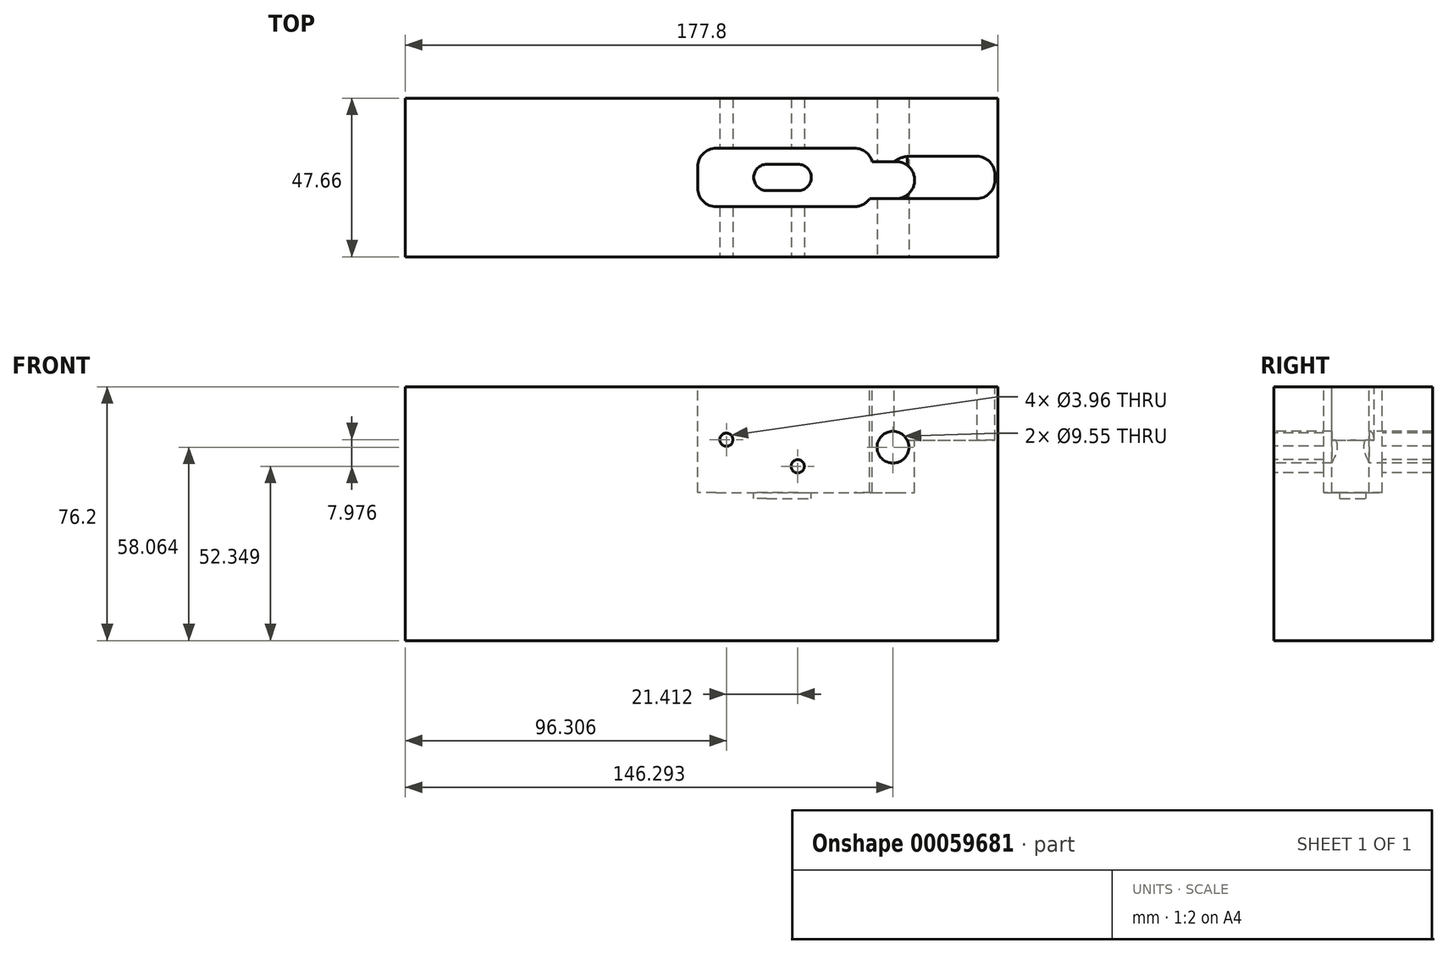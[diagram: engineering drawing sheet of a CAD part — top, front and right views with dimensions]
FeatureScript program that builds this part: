
annotation { "Feature Type Name" : "Feature", "Feature Type Description" : "" }
export const myFeature = defineFeature(function(context is Context, id is Id, definition is map)
    precondition{}
    {
        {
            var Q0;
            Q0=qCreatedBy(makeId("Top.planeOp"),FACE);
            var sketch = newSketch(context, id + "F0", { "sketchPlane" : qUnion([Q0])});
            skLineSegment(sketch, "E0.bottom", {"start": v(0.01, 76.23) * mm, "end": v(177.81, 76.23) * mm});
            skLineSegment(sketch, "E0.top", {"start": v(0.01, 28.58) * mm, "end": v(177.81, 28.58) * mm});
            skLineSegment(sketch, "E0.left", {"start": v(0.01, 76.23) * mm, "end": v(0.01, 28.58) * mm});
            skLineSegment(sketch, "E0.right", {"start": v(177.81, 76.23) * mm, "end": v(177.81, 28.58) * mm});
            skLineSegment(sketch, "E1", {"start": v(177.78, 52.4) * mm, "end": v(-20.58, 52.4) * mm, "construction": true});
            skPoint(sketch, "E1.startSnap0", {"position": v(177.81, 52.4) * mm});
            skPoint(sketch, "E1.endSnap0", {"position": v(0.01, 52.4) * mm});
            skSolve(sketch);
        }
        {
            var Q0;
            Q0=makeQuery(id+"F0.imprint","IMPRINT",FACE,{"disambiguationData":[TD([[makeQuery(id+"F0.imprint","IMPRINT",EDGE,{"derivedFrom":sQuery(id+"F0.wireOp",EDGE,"E0.bottom")}),-1.0]])]});
            extrude(context, id + "F1", {"entities" : qUnion([Q0]), "depth" : 76.2 * mm});
        }
        {
            var Q0;
            Q0=makeQuery(id+"F1.opExtrude","SWEPT_FACE",FACE,{"disambiguationData":[OSD([sQuery(id+"F0.wireOp",EDGE,"E0.top")])]});
            var sketch = newSketch(context, id + "F2", { "sketchPlane" : qUnion([Q0])});
            skCircle(sketch, "E2", {"center": v(166.7, 69.85) * mm, "radius": 3.18 * mm, "construction": true});
            skCircle(sketch, "E3", {"center": v(4.77, 69.85) * mm, "radius": 3.18 * mm, "construction": true});
            skCircle(sketch, "E4", {"center": v(146.3, 58.06) * mm, "radius": 4.78 * mm});
            skCircle(sketch, "E5", {"center": v(117.73, 52.35) * mm, "radius": 1.98 * mm});
            skCircle(sketch, "E6", {"center": v(96.32, 60.33) * mm, "radius": 1.98 * mm});
            skPoint(sketch, "E7", {"position": v(0.01, 76.2) * mm});
            skSolve(sketch);
        }
        {
            var Q0;
            Q0=qSketchRegion(id+"F2",true);
            extrude(context, id + "F3", {"entities" : qUnion([Q0]), "operationType" : NewBodyOperationType.REMOVE, "endBound" : BoundingType.THROUGH_ALL, "oppositeDirection" : true, "depth" : 25.4 * mm});
        }
        {
            var Q0;
            Q0=makeQuery(id+"F1.opExtrude","CAP_FACE",FACE,{"disambiguationData":[OSD([sQuery(id+"F0.wireOp",EDGE,"E0.bottom"),sQuery(id+"F0.wireOp",EDGE,"E0.top"),sQuery(id+"F0.wireOp",EDGE,"E0.left"),sQuery(id+"F0.wireOp",EDGE,"E0.right")])],"isStart":false});
            var sketch = newSketch(context, id + "F4", { "sketchPlane" : qUnion([Q0])});
            skLineSegment(sketch, "E8.right", {"start": v(176.91, 53.21) * mm, "end": v(176.91, 51.59) * mm});
            skPoint(sketch, "E9.visualSharp", {"position": v(176.91, 58.75) * mm});
            skArc(sketch, "E9.filletArc", {"start": v(176.91, 53.21) * mm, "mid": v(175.33, 57.09) * mm, "end": v(171.49, 58.75) * mm});
            skPoint(sketch, "E10.visualSharp", {"position": v(176.91, 46.05) * mm});
            skArc(sketch, "E10.filletArc", {"start": v(171.39, 46.05) * mm, "mid": v(175.3, 47.68) * mm, "end": v(176.91, 51.59) * mm});
            skPoint(sketch, "E11.visualSharp", {"position": v(142.53, 46.05) * mm});
            skLineSegment(sketch, "E12", {"start": v(142.53, 46.05) * mm, "end": v(142.53, 46.05) * mm});
            skLineSegment(sketch, "E13", {"start": v(151.35, 58.75) * mm, "end": v(171.49, 58.75) * mm});
            skLineSegment(sketch, "E14", {"start": v(4.77, 92.25) * mm, "end": v(4.77, 28.58) * mm, "construction": true});
            skLineSegment(sketch, "E15", {"start": v(149.26, 58.75) * mm, "end": v(149.26, 58.75) * mm});
            skLineSegment(sketch, "E16", {"start": v(143.73, 51.13) * mm, "end": v(143.73, 49.23) * mm});
            skLineSegment(sketch, "E17", {"start": v(146.9, 46.05) * mm, "end": v(171.39, 46.05) * mm});
            skPoint(sketch, "E18.visualSharp", {"position": v(143.73, 58.75) * mm});
            skPoint(sketch, "E19.visualSharp", {"position": v(143.73, 46.05) * mm});
            skArc(sketch, "E19.filletArc", {"start": v(143.73, 49.23) * mm, "mid": v(144.66, 46.98) * mm, "end": v(146.9, 46.05) * mm});
            skPoint(sketch, "E20.newPointA", {"position": v(149.26, 58.75) * mm});
            skArc(sketch, "E20.filletArc", {"start": v(151.35, 58.75) * mm, "mid": v(145.96, 56.52) * mm, "end": v(143.73, 51.13) * mm});
            skSolve(sketch);
        }
        {
            var Q0;
            Q0=qSketchRegion(id+"F4",true);
            extrude(context, id + "F5", {"entities" : qUnion([Q0]), "operationType" : NewBodyOperationType.REMOVE, "oppositeDirection" : true, "depth" : 16 * mm});
        }
        {
            var Q0;
            Q0=makeQuery(id+"F1.opExtrude","CAP_FACE",FACE,{"disambiguationData":[OSD([sQuery(id+"F0.wireOp",EDGE,"E0.bottom"),sQuery(id+"F0.wireOp",EDGE,"E0.top"),sQuery(id+"F0.wireOp",EDGE,"E0.left"),sQuery(id+"F0.wireOp",EDGE,"E0.right")])],"isStart":false});
            var sketch = newSketch(context, id + "F6", { "sketchPlane" : qUnion([Q0])});
            skLineSegment(sketch, "E21.bottom", {"start": v(108.48, 56.36) * mm, "end": v(117.83, 56.36) * mm});
            skLineSegment(sketch, "E21.top", {"start": v(108.48, 48.44) * mm, "end": v(117.83, 48.44) * mm});
            skLineSegment(sketch, "E21.left", {"start": v(104.52, 52.4) * mm, "end": v(104.52, 52.4) * mm});
            skLineSegment(sketch, "E21.right", {"start": v(121.8, 52.4) * mm, "end": v(121.8, 52.4) * mm});
            skPoint(sketch, "E22.visualSharp", {"position": v(104.52, 56.36) * mm});
            skArc(sketch, "E22.filletArc", {"start": v(108.48, 56.36) * mm, "mid": v(105.68, 55.2) * mm, "end": v(104.52, 52.4) * mm});
            skPoint(sketch, "E23.visualSharp", {"position": v(121.8, 56.36) * mm});
            skArc(sketch, "E23.filletArc", {"start": v(121.8, 52.4) * mm, "mid": v(120.63, 55.2) * mm, "end": v(117.83, 56.36) * mm});
            skPoint(sketch, "E24.visualSharp", {"position": v(121.8, 48.44) * mm});
            skArc(sketch, "E24.filletArc", {"start": v(117.83, 48.44) * mm, "mid": v(120.63, 49.6) * mm, "end": v(121.8, 52.4) * mm});
            skPoint(sketch, "E25.visualSharp", {"position": v(104.52, 48.44) * mm});
            skArc(sketch, "E25.filletArc", {"start": v(104.52, 52.4) * mm, "mid": v(105.68, 49.6) * mm, "end": v(108.48, 48.44) * mm});
            skSolve(sketch);
        }
        {
            var Q0;
            Q0=qSketchRegion(id+"F6",true);
            extrude(context, id + "F7", {"entities" : qUnion([Q0]), "operationType" : NewBodyOperationType.REMOVE, "oppositeDirection" : true, "depth" : 33.53 * mm});
        }
        {
            var Q0;
            Q0=makeQuery(id+"F1.opExtrude","CAP_FACE",FACE,{"disambiguationData":[OSD([sQuery(id+"F0.wireOp",EDGE,"E0.bottom"),sQuery(id+"F0.wireOp",EDGE,"E0.top"),sQuery(id+"F0.wireOp",EDGE,"E0.left"),sQuery(id+"F0.wireOp",EDGE,"E0.right")])],"isStart":false});
            var sketch = newSketch(context, id + "F8", { "sketchPlane" : qUnion([Q0])});
            skLineSegment(sketch, "E26", {"start": v(-7.04, 52.4) * mm, "end": v(179.84, 52.4) * mm, "construction": true});
            skLineSegment(sketch, "E27.bottom", {"start": v(93.24, 61.16) * mm, "end": v(134.77, 61.16) * mm});
            skLineSegment(sketch, "E27.top", {"start": v(93.24, 43.64) * mm, "end": v(134.77, 43.64) * mm});
            skLineSegment(sketch, "E27.left", {"start": v(87.7, 55.63) * mm, "end": v(87.7, 49.17) * mm});
            skLineSegment(sketch, "E27.right", {"start": v(140.3, 55.63) * mm, "end": v(140.3, 49.17) * mm});
            skLineSegment(sketch, "E28.left", {"start": v(152.8, 51.59) * mm, "end": v(152.8, 51.64) * mm});
            skLineSegment(sketch, "E28.right", {"start": v(129.37, 51.59) * mm, "end": v(129.37, 51.64) * mm});
            skPoint(sketch, "E29.visualSharp", {"position": v(140.3, 61.16) * mm});
            skArc(sketch, "E29.filletArc", {"start": v(140.3, 55.63) * mm, "mid": v(138.69, 59.54) * mm, "end": v(134.77, 61.16) * mm});
            skPoint(sketch, "E30.visualSharp", {"position": v(140.3, 43.64) * mm});
            skArc(sketch, "E30.filletArc", {"start": v(134.77, 43.64) * mm, "mid": v(138.69, 45.26) * mm, "end": v(140.3, 49.17) * mm});
            skPoint(sketch, "E31.visualSharp", {"position": v(87.7, 61.16) * mm});
            skArc(sketch, "E31.filletArc", {"start": v(93.24, 61.16) * mm, "mid": v(89.33, 59.54) * mm, "end": v(87.7, 55.63) * mm});
            skPoint(sketch, "E32.visualSharp", {"position": v(87.7, 43.64) * mm});
            skArc(sketch, "E32.filletArc", {"start": v(87.7, 49.17) * mm, "mid": v(89.33, 45.26) * mm, "end": v(93.24, 43.64) * mm});
            skSolve(sketch);
        }
        {
            var Q0;
            Q0=qSketchRegion(id+"F8",true);
            extrude(context, id + "F9", {"entities" : qUnion([Q0]), "operationType" : NewBodyOperationType.REMOVE, "oppositeDirection" : true, "depth" : 31.72 * mm});
        }
        {
            var Q0;
            Q0=makeQuery(id+"F8.imprint","IMPRINT",FACE,{"disambiguationData":[TD([[makeQuery(id+"F8.imprint","IMPRINT",EDGE,{"derivedFrom":sQuery(id+"F8.wireOp",EDGE,"E27.bottom")}),1.0]])]});
            var sketch = newSketch(context, id + "F10", { "sketchPlane" : qUnion([Q0])});
            skLineSegment(sketch, "E33.bottom", {"start": v(139.35, 57.18) * mm, "end": v(147.24, 57.18) * mm});
            skLineSegment(sketch, "E33.top", {"start": v(139.35, 46.05) * mm, "end": v(147.24, 46.05) * mm});
            skLineSegment(sketch, "E33.left", {"start": v(136.17, 54) * mm, "end": v(136.17, 49.23) * mm});
            skLineSegment(sketch, "E33.right", {"start": v(152.78, 51.64) * mm, "end": v(152.78, 51.59) * mm});
            skPoint(sketch, "E34.visualSharp", {"position": v(152.78, 57.18) * mm});
            skArc(sketch, "E34.filletArc", {"start": v(152.78, 51.64) * mm, "mid": v(151.16, 55.55) * mm, "end": v(147.24, 57.18) * mm});
            skPoint(sketch, "E35.visualSharp", {"position": v(152.78, 46.05) * mm});
            skArc(sketch, "E35.filletArc", {"start": v(147.24, 46.05) * mm, "mid": v(151.16, 47.67) * mm, "end": v(152.78, 51.59) * mm});
            skPoint(sketch, "E36.visualSharp", {"position": v(136.17, 57.18) * mm});
            skArc(sketch, "E36.filletArc", {"start": v(139.35, 57.18) * mm, "mid": v(137.1, 56.25) * mm, "end": v(136.17, 54) * mm});
            skPoint(sketch, "E37.visualSharp", {"position": v(136.17, 46.05) * mm});
            skArc(sketch, "E37.filletArc", {"start": v(136.17, 49.23) * mm, "mid": v(137.1, 46.98) * mm, "end": v(139.35, 46.05) * mm});
            skSolve(sketch);
        }
        {
            var Q0;
            Q0 = qSketchRegion(id + "F10", true);
            extrude(context, id + "F11", {"entities" : qUnion([Q0]), "operationType" : NewBodyOperationType.REMOVE, "oppositeDirection" : true, "depth" : 31.72 * mm});
        }
    });
